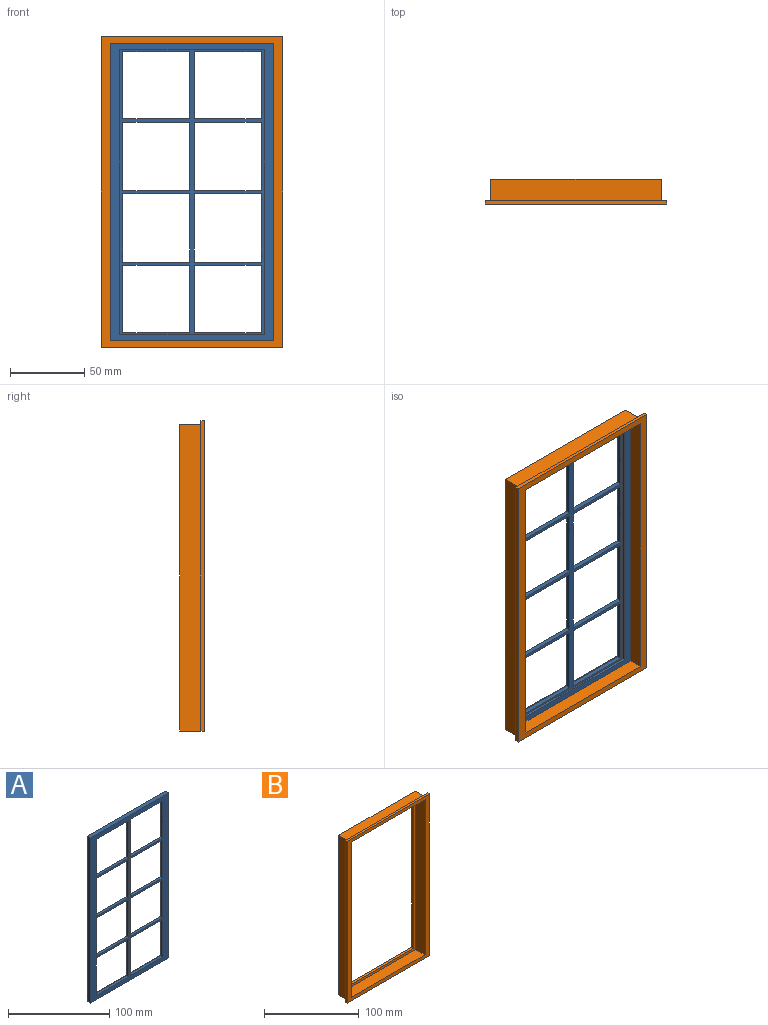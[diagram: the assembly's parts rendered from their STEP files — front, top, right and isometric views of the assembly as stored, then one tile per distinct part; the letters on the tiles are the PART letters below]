
ASSEMBLY  parts=2 mates=1
PART A: 43 faces, bbox 109.1x4.8x199.5 mm
  f0: plane 96.84x1.59mm, normal (0,0,1), area 153.7mm2, adj f1,f3,f4,f5
  f1: plane 191.56x1.59mm, normal (1,0,0), area 304.1mm2, adj f0,f2,f4,f5
  f2: plane 96.84x1.59mm, normal (0,0,-1), area 153.7mm2, adj f1,f3,f4,f5
  f3: plane 191.56x1.59mm, normal (-1,0,0), area 304.1mm2, adj f0,f2,f4,f5
  f4: plane 199.53x109.11mm, normal (0,1,0), area 3220.4mm2, adj f0,f1,f2,f3,f6,f7,f8,f9
  f5: plane 191.56x96.84mm, normal (0,1,0), area 2139mm2, adj f0,f1,f2,f3,f10,f11,f12,f13
  f6: plane 109.11x4.76mm, normal (0,0,1), area 519.6mm2, adj f4,f7,f9,f42
  f7: plane 199.53x4.76mm, normal (-1,0,0), area 950.3mm2, adj f4,f6,f8,f42
  f8: plane 109.11x4.76mm, normal (0,0,-1), area 519.6mm2, adj f4,f7,f9,f42
  f9: plane 199.53x4.76mm, normal (1,0,0), area 950.3mm2, adj f4,f6,f8,f42
  f10: plane 45.97x3.18mm, normal (1,0,0), area 146mm2, adj f5,f11,f13,f42
  f11: plane 44.91x3.18mm, normal (0,0,-1), area 142.6mm2, adj f5,f10,f12,f42
  f12: plane 45.97x3.18mm, normal (-1,0,0), area 146mm2, adj f5,f11,f13,f42
  f13: plane 44.91x3.18mm, normal (0,0,1), area 142.6mm2, adj f5,f10,f12,f42
  f14: plane 45.97x3.18mm, normal (1,0,0), area 146mm2, adj f5,f15,f17,f42
  f15: plane 44.91x3.18mm, normal (0,0,-1), area 142.6mm2, adj f5,f14,f16,f42
  f16: plane 45.97x3.18mm, normal (-1,0,0), area 146mm2, adj f5,f15,f17,f42
  f17: plane 44.91x3.18mm, normal (0,0,1), area 142.6mm2, adj f5,f14,f16,f42
  f18: plane 44.91x3.18mm, normal (0,0,1), area 142.6mm2, adj f5,f19,f21,f42
  f19: plane 45.97x3.18mm, normal (1,0,0), area 146mm2, adj f5,f18,f20,f42
  f20: plane 44.91x3.18mm, normal (0,0,-1), area 142.6mm2, adj f5,f19,f21,f42
  f21: plane 45.97x3.18mm, normal (-1,0,0), area 146mm2, adj f5,f18,f20,f42
  f22: plane 45.97x3.18mm, normal (-1,0,0), area 146mm2, adj f5,f23,f25,f42
  f23: plane 44.91x3.18mm, normal (0,0,1), area 142.6mm2, adj f5,f22,f24,f42
  f24: plane 45.97x3.18mm, normal (1,0,0), area 146mm2, adj f5,f23,f25,f42
  f25: plane 44.91x3.18mm, normal (0,0,-1), area 142.6mm2, adj f5,f22,f24,f42
  f26: plane 45.44x3.18mm, normal (1,0,0), area 144.3mm2, adj f5,f27,f29,f42
  f27: plane 44.91x3.18mm, normal (0,0,-1), area 142.6mm2, adj f5,f26,f28,f42
  f28: plane 45.44x3.18mm, normal (-1,0,0), area 144.3mm2, adj f5,f27,f29,f42
  f29: plane 44.91x3.18mm, normal (0,0,1), area 142.6mm2, adj f5,f26,f28,f42
  f30: plane 45.44x3.18mm, normal (-1,0,0), area 144.3mm2, adj f5,f31,f33,f42
  f31: plane 44.91x3.18mm, normal (0,0,1), area 142.6mm2, adj f5,f30,f32,f42
  f32: plane 45.44x3.18mm, normal (1,0,0), area 144.3mm2, adj f5,f31,f33,f42
  f33: plane 44.91x3.18mm, normal (0,0,-1), area 142.6mm2, adj f5,f30,f32,f42
  f34: plane 44.91x3.18mm, normal (0,0,1), area 142.6mm2, adj f5,f35,f37,f42
  f35: plane 45.31x3.18mm, normal (1,0,0), area 143.9mm2, adj f5,f34,f36,f42
  f36: plane 44.91x3.18mm, normal (0,0,-1), area 142.6mm2, adj f5,f35,f37,f42
  f37: plane 45.31x3.18mm, normal (-1,0,0), area 143.9mm2, adj f5,f34,f36,f42
  f38: plane 44.91x3.18mm, normal (0,0,-1), area 142.6mm2, adj f5,f39,f41,f42
  f39: plane 45.31x3.18mm, normal (-1,0,0), area 143.9mm2, adj f5,f38,f40,f42
  f40: plane 44.91x3.18mm, normal (0,0,1), area 142.6mm2, adj f5,f39,f41,f42
  f41: plane 45.31x3.18mm, normal (1,0,0), area 143.9mm2, adj f5,f38,f40,f42
  f42: plane 199.53x109.11mm, normal (0,-1,0), area 5359.4mm2, adj f6,f7,f8,f9,f10,f11,f12,f13
PART B: 19 faces, bbox 122.2x16.7x208.5 mm
  f0: plane 200.03x13.67mm, normal (-1,0,0), area 2734.1mm2, adj f9,f10,f11,f18
  f1: plane 208.49x122.24mm, normal (0,1,0), area 1957mm2, adj f2,f3,f4,f5,f6,f7,f8
  f2: plane 208.49x2.38mm, normal (-1,0,0), area 496.5mm2, adj f1,f3,f5,f10
  f3: plane 122.24x2.38mm, normal (0,0,1), area 291.1mm2, adj f1,f2,f4,f10
  f4: plane 208.49x2.38mm, normal (1,0,0), area 496.5mm2, adj f1,f3,f5,f10
  f5: plane 122.24x16.67mm, normal (0,0,-1), area 1924.1mm2, adj f1,f2,f4,f6,f7,f10,f12
  f6: plane 205.85x14.29mm, normal (-1,0,0), area 2941mm2, adj f1,f5,f8,f12
  f7: plane 205.85x14.29mm, normal (1,0,0), area 2941mm2, adj f1,f5,f8,f12
  f8: plane 114.3x14.29mm, normal (0,0,1), area 1633.1mm2, adj f1,f6,f7,f12
  f9: plane 109.54x13.67mm, normal (0,0,1), area 1497.2mm2, adj f0,f10,f13,f18
  f10: plane 208.49x122.24mm, normal (0,-1,0), area 3575.3mm2, adj f0,f2,f3,f4,f5,f9,f11,f13
  f11: plane 109.54x13.67mm, normal (0,0,-1), area 1497.2mm2, adj f0,f10,f13,f18
  f12: plane 205.85x114.3mm, normal (0,1,0), area 3439.3mm2, adj f5,f6,f7,f8,f14,f15,f16,f17
  f13: plane 200.03x13.67mm, normal (1,0,0), area 2734.1mm2, adj f9,f10,f11,f18
  f14: plane 103.54x3mm, normal (0,0,-1), area 310.6mm2, adj f12,f15,f17,f18
  f15: plane 194.03x3mm, normal (1,0,0), area 582.1mm2, adj f12,f14,f16,f18
  f16: plane 103.54x3mm, normal (0,0,1), area 310.6mm2, adj f12,f15,f17,f18
  f17: plane 194.03x3mm, normal (-1,0,0), area 582.1mm2, adj f12,f14,f16,f18
  f18: plane 200.03x109.54mm, normal (0,-1,0), area 1821.4mm2, adj f0,f9,f11,f13,f14,f15,f16,f17
PLACE A rot(axis=(0,0,1),180deg) t=(191.96,-8.95,-65.16)mm
PLACE B t=(64.1,22.62,-65.09)mm
MATE fastened B.f18 <-> A.f42  axis (0,-1,0) through (6.35,13.67,204.26)mm
